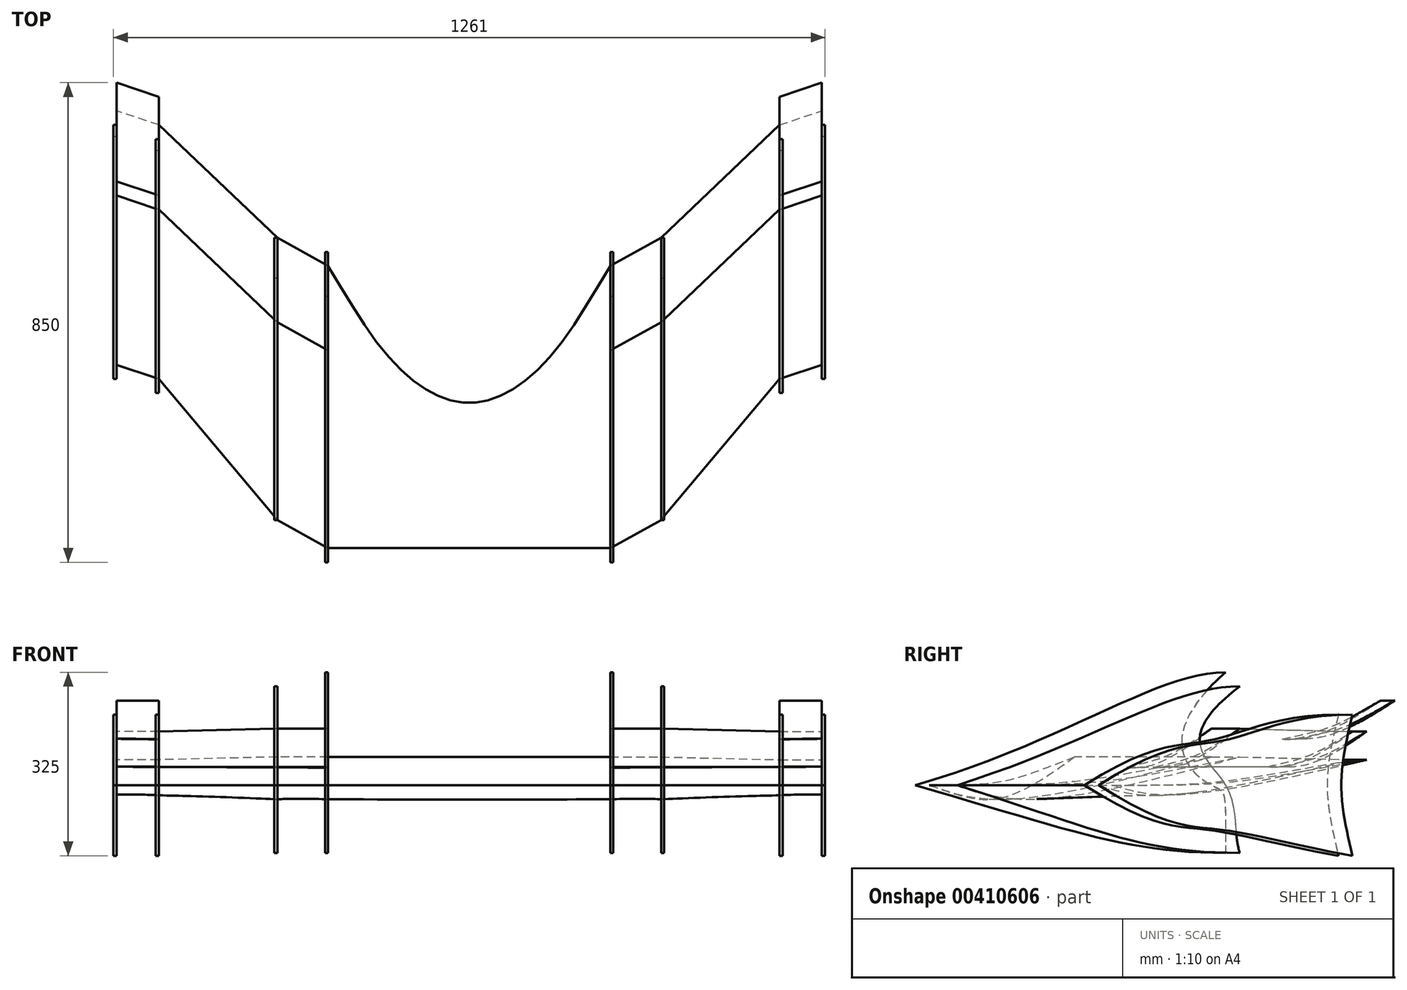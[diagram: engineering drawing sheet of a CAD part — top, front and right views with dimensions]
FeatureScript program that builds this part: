
annotation { "Feature Type Name" : "Feature", "Feature Type Description" : "" }
export const myFeature = defineFeature(function(context is Context, id is Id, definition is map)
    precondition{}
    {
        {
            var Q0;
            Q0=qCreatedBy(makeId("Right.planeOp"),FACE);
            cPlane(context, id + "F0", {"entities" : qUnion([Q0]), "cplaneType" : CPlaneType.OFFSET, "offset" : 250 * mm, "width" : 150 * mm, "height" : 150 * mm});
        }
        {
            var Q0;
            Q0=qCreatedBy(id+"F0.planeOp",FACE);
            var sketch = newSketch(context, id + "F1", { "sketchPlane" : qUnion([Q0])});
            skPoint(sketch, "E0.middle", {"position": v(0, 0) * mm});
            skFitSpline(sketch, "E1", {"points": [v(-275, 0) * mm, v(275, 200) * mm], "startDerivative": vector(825, 240) * mm, "endDerivative": vector(375, 0) * mm});
            skFitSpline(sketch, "E2", {"points": [v(275, 200) * mm, v(250, 0) * mm, v(275, -120) * mm], "startDerivative": vector(-734.18, -640.74) * mm, "endDerivative": vector(0, -821.63) * mm});
            skFitSpline(sketch, "E3", {"points": [v(-275, 0) * mm, v(275, -120) * mm], "startDerivative": vector(825, -240) * mm, "endDerivative": vector(525, 0) * mm});
            skSolve(sketch);
        }
        {
            var Q0;
            Q0=qCreatedBy(makeId("Right.planeOp"),FACE);
            cPlane(context, id + "F2", {"entities" : qUnion([Q0]), "cplaneType" : CPlaneType.OFFSET, "offset" : 340 * mm, "width" : 150 * mm, "height" : 150 * mm});
        }
        {
            var Q0;
            Q0=qCreatedBy(id+"F2.planeOp",FACE);
            var sketch = newSketch(context, id + "F3", { "sketchPlane" : qUnion([Q0])});
            skFitSpline(sketch, "E4", {"points": [v(-200, 0) * mm, v(300, 175) * mm], "startDerivative": vector(750, 240) * mm, "endDerivative": vector(375, 0) * mm});
            skFitSpline(sketch, "E5", {"points": [v(300, 175) * mm, v(275, 0) * mm, v(300, -120) * mm], "startDerivative": vector(-687.26, -522.32) * mm, "endDerivative": vector(77.93, -251.25) * mm});
            skFitSpline(sketch, "E6", {"points": [v(-200, 0) * mm, v(300, -120) * mm], "startDerivative": vector(750, -240) * mm, "endDerivative": vector(525, 0) * mm});
            skSolve(sketch);
        }
        {
            var Q0;
            Q0=qCreatedBy(makeId("Right.planeOp"),FACE);
            cPlane(context, id + "F4", {"entities" : qUnion([Q0]), "cplaneType" : CPlaneType.OFFSET, "offset" : 550 * mm, "width" : 150 * mm, "height" : 150 * mm});
        }
        {
            var Q0;
            Q0=qCreatedBy(id+"F4.planeOp",FACE);
            var sketch = newSketch(context, id + "F5", { "sketchPlane" : qUnion([Q0])});
            skFitSpline(sketch, "E7", {"points": [v(25, 0) * mm, v(250, 80) * mm, v(475, 125) * mm], "startDerivative": vector(742.6, 475.26) * mm, "endDerivative": vector(681.8, 0) * mm});
            skFitSpline(sketch, "E8", {"points": [v(475, 125) * mm, v(455, 0) * mm, v(475, -125) * mm], "startDerivative": vector(-60, -250) * mm, "endDerivative": vector(60, -250) * mm});
            skFitSpline(sketch, "E9", {"points": [v(25, 0) * mm, v(250, -80) * mm, v(475, -125) * mm], "startDerivative": vector(742.6, -475.26) * mm, "endDerivative": vector(456.76, -74.2) * mm});
            skSolve(sketch);
        }
        {
            var Q0;
            Q0=qCreatedBy(makeId("Right.planeOp"),FACE);
            cPlane(context, id + "F6", {"entities" : qUnion([Q0]), "cplaneType" : CPlaneType.OFFSET, "offset" : 625 * mm, "width" : 150 * mm, "height" : 150 * mm});
        }
        {
            var Q0;
            Q0=qCreatedBy(id+"F6.planeOp",FACE);
            var sketch = newSketch(context, id + "F7", { "sketchPlane" : qUnion([Q0])});
            skFitSpline(sketch, "E10", {"points": [v(50, 0) * mm, v(275, 80) * mm, v(500, 125) * mm], "startDerivative": vector(742.6, 475.26) * mm, "endDerivative": vector(681.8, 0) * mm});
            skFitSpline(sketch, "E11", {"points": [v(500, 125) * mm, v(480, 0) * mm, v(500, -125) * mm], "startDerivative": vector(-60, -250) * mm, "endDerivative": vector(60, -250) * mm});
            skFitSpline(sketch, "E12", {"points": [v(50, 0) * mm, v(275, -80) * mm, v(500, -125) * mm], "startDerivative": vector(742.6, -475.26) * mm, "endDerivative": vector(456.76, -74.2) * mm});
            skSolve(sketch);
        }
        {
            var Q0;
            Q0=qCreatedBy(makeId("Right.planeOp"),FACE);
            cPlane(context, id + "F8", {"entities" : qUnion([Q0]), "cplaneType" : CPlaneType.OFFSET, "offset" : 160 * mm, "width" : 150 * mm, "height" : 150 * mm});
        }
        {
            var Q0;
            Q0=qCreatedBy(id+"F8.planeOp",FACE);
            var sketch = newSketch(context, id + "F9", { "sketchPlane" : qUnion([Q0])});
            skFitSpline(sketch, "E13", {"points": [v(-250, 0) * mm, v(-125, -25) * mm, v(110, 50) * mm], "startDerivative": vector(276.92, -99.23) * mm, "endDerivative": vector(434.5, 183.8) * mm});
            skFitSpline(sketch, "E14", {"points": [v(-250, 0) * mm, v(110, 50) * mm], "startDerivative": vector(540, 0) * mm, "endDerivative": vector(540, 150) * mm});
            skSolve(sketch);
        }
        {
            var Q0;
            Q0=qCreatedBy(makeId("Right.planeOp"),FACE);
            cPlane(context, id + "F10", {"entities" : qUnion([Q0]), "cplaneType" : CPlaneType.OFFSET, "offset" : 250 * mm, "width" : 150 * mm, "height" : 150 * mm});
        }
        {
            var Q0;
            Q0=qCreatedBy(id+"F10.planeOp",FACE);
            var sketch = newSketch(context, id + "F11", { "sketchPlane" : qUnion([Q0])});
            skFitSpline(sketch, "E15", {"points": [v(-250, 0) * mm, v(-125, -25) * mm, v(250, 50) * mm], "startDerivative": vector(295.75, -102.45) * mm, "endDerivative": vector(670.75, 177.45) * mm});
            skFitSpline(sketch, "E16", {"points": [v(-250, 0) * mm, v(250, 50) * mm], "startDerivative": vector(750, 0) * mm, "endDerivative": vector(750, 150) * mm});
            skSolve(sketch);
        }
        {
            var Q0;
            Q0=qCreatedBy(id+"F10.planeOp",FACE);
            var sketch = newSketch(context, id + "F12", { "sketchPlane" : qUnion([Q0])});
            skFitSpline(sketch, "E17", {"points": [v(100, 32) * mm, v(125, 32) * mm, v(250, 100) * mm], "startDerivative": vector(70.95, -14.25) * mm, "endDerivative": vector(319.3, 251.19) * mm});
            skFitSpline(sketch, "E18", {"points": [v(100, 32) * mm, v(250, 100) * mm], "startDerivative": vector(225, 54) * mm, "endDerivative": vector(225, 150) * mm});
            skSolve(sketch);
        }
        {
            var Q0;
            Q0=qCreatedBy(makeId("Right.planeOp"),FACE);
            cPlane(context, id + "F13", {"entities" : qUnion([Q0]), "cplaneType" : CPlaneType.OFFSET, "offset" : 340 * mm, "width" : 150 * mm, "height" : 150 * mm});
        }
        {
            var Q0;
            Q0=qCreatedBy(id+"F13.planeOp",FACE);
            var sketch = newSketch(context, id + "F14", { "sketchPlane" : qUnion([Q0])});
            skFitSpline(sketch, "E19", {"points": [v(-200, 0) * mm, v(-75, -25) * mm, v(300, 50) * mm], "startDerivative": vector(295.75, -102.45) * mm, "endDerivative": vector(670.75, 177.45) * mm});
            skFitSpline(sketch, "E20", {"points": [v(-200, 0) * mm, v(300, 50) * mm], "startDerivative": vector(750, 0) * mm, "endDerivative": vector(750, 150) * mm});
            skSolve(sketch);
        }
        {
            var Q0;
            Q0=qCreatedBy(id+"F13.planeOp",FACE);
            var sketch = newSketch(context, id + "F15", { "sketchPlane" : qUnion([Q0])});
            skFitSpline(sketch, "E21", {"points": [v(150, 32.5) * mm, v(175, 32.5) * mm, v(300, 100) * mm], "startDerivative": vector(70.88, -14.16) * mm, "endDerivative": vector(319.39, 250.19) * mm});
            skFitSpline(sketch, "E22", {"points": [v(150, 32.5) * mm, v(300, 100) * mm], "startDerivative": vector(225, 52.5) * mm, "endDerivative": vector(225, 150) * mm});
            skSolve(sketch);
        }
        {
            var Q0;
            Q0=qCreatedBy(makeId("Right.planeOp"),FACE);
            cPlane(context, id + "F16", {"entities" : qUnion([Q0]), "cplaneType" : CPlaneType.OFFSET, "offset" : 550 * mm, "width" : 150 * mm, "height" : 150 * mm});
        }
        {
            var Q0;
            Q0=qCreatedBy(id+"F16.planeOp",FACE);
            var sketch = newSketch(context, id + "F17", { "sketchPlane" : qUnion([Q0])});
            skFitSpline(sketch, "E23", {"points": [v(50, 0) * mm, v(150, -18) * mm, v(500, 45) * mm], "startDerivative": vector(243.54, -77.51) * mm, "endDerivative": vector(618.54, 145.01) * mm});
            skFitSpline(sketch, "E24", {"points": [v(50, 0) * mm, v(500, 45) * mm], "startDerivative": vector(600, 0) * mm, "endDerivative": vector(750, 135) * mm});
            skSolve(sketch);
        }
        {
            var Q0;
            Q0=qCreatedBy(id+"F16.planeOp",FACE);
            var sketch = newSketch(context, id + "F18", { "sketchPlane" : qUnion([Q0])});
            skFitSpline(sketch, "E25", {"points": [v(350, 33) * mm, v(375, 33) * mm, v(500, 95) * mm], "startDerivative": vector(70.1, -13.12) * mm, "endDerivative": vector(320.24, 228.44) * mm});
            skFitSpline(sketch, "E26", {"points": [v(350, 33) * mm, v(500, 95) * mm], "startDerivative": vector(225, 51) * mm, "endDerivative": vector(225, 135) * mm});
            skSolve(sketch);
        }
        {
            var Q0;
            Q0=qCreatedBy(id+"F16.planeOp",FACE);
            var sketch = newSketch(context, id + "F19", { "sketchPlane" : qUnion([Q0])});
            skFitSpline(sketch, "E27", {"points": [v(375, 82) * mm, v(400, 82) * mm, v(550, 150) * mm], "startDerivative": vector(72.45, -13.25) * mm, "endDerivative": vector(364.77, 245.96) * mm});
            skFitSpline(sketch, "E28", {"points": [v(375, 82) * mm, v(550, 150) * mm], "startDerivative": vector(262.5, 54) * mm, "endDerivative": vector(262.5, 150) * mm});
            skSolve(sketch);
        }
        {
            var Q0;
            Q0=qCreatedBy(makeId("Right.planeOp"),FACE);
            cPlane(context, id + "F20", {"entities" : qUnion([Q0]), "cplaneType" : CPlaneType.OFFSET, "offset" : 625 * mm, "width" : 150 * mm, "height" : 150 * mm});
        }
        {
            var Q0;
            Q0=qCreatedBy(id+"F20.planeOp",FACE);
            var sketch = newSketch(context, id + "F21", { "sketchPlane" : qUnion([Q0])});
            skFitSpline(sketch, "E29", {"points": [v(75, 0) * mm, v(175, -17) * mm, v(525, 45) * mm], "startDerivative": vector(243.71, -73.88) * mm, "endDerivative": vector(618.37, 142.03) * mm});
            skFitSpline(sketch, "E30", {"points": [v(75, 0) * mm, v(525, 45) * mm], "startDerivative": vector(600, 0) * mm, "endDerivative": vector(750, 135) * mm});
            skSolve(sketch);
        }
        {
            var Q0;
            Q0=qCreatedBy(id+"F20.planeOp",FACE);
            var sketch = newSketch(context, id + "F22", { "sketchPlane" : qUnion([Q0])});
            skFitSpline(sketch, "E31", {"points": [v(375, 33.5) * mm, v(400, 33.5) * mm, v(525, 95) * mm], "startDerivative": vector(70.04, -13.03) * mm, "endDerivative": vector(320.32, 227.42) * mm});
            skFitSpline(sketch, "E32", {"points": [v(375, 33.5) * mm, v(525, 95) * mm], "startDerivative": vector(225, 49.5) * mm, "endDerivative": vector(225, 135) * mm});
            skSolve(sketch);
        }
        {
            var Q0;
            Q0=qCreatedBy(id+"F20.planeOp",FACE);
            var sketch = newSketch(context, id + "F23", { "sketchPlane" : qUnion([Q0])});
            skFitSpline(sketch, "E33", {"points": [v(400, 83) * mm, v(425, 83) * mm, v(575, 150) * mm], "startDerivative": vector(72.33, -13.07) * mm, "endDerivative": vector(364.9, 243.96) * mm});
            skFitSpline(sketch, "E34", {"points": [v(400, 83) * mm, v(575, 150) * mm], "startDerivative": vector(262.5, 51) * mm, "endDerivative": vector(262.5, 150) * mm});
            skSolve(sketch);
        }
        {
            var Q0;
            Q0=qCreatedBy(makeId("Right.planeOp"),FACE);
            cPlane(context, id + "F24", {"entities" : qUnion([Q0]), "cplaneType" : CPlaneType.OFFSET, "offset" : 250 * mm, "oppositeDirection" : true, "width" : 150 * mm, "height" : 150 * mm});
        }
        {
            var Q0;
            Q0=qCreatedBy(id+"F24.planeOp",FACE);
            var sketch = newSketch(context, id + "F25", { "sketchPlane" : qUnion([Q0])});
            skPoint(sketch, "E35.middle", {"position": v(0, 0) * mm});
            skFitSpline(sketch, "E36", {"points": [v(-275, 0) * mm, v(275, 200) * mm], "startDerivative": vector(825, 240) * mm, "endDerivative": vector(375, 0) * mm});
            skFitSpline(sketch, "E37", {"points": [v(275, 200) * mm, v(250, 0) * mm, v(275, -120) * mm], "startDerivative": vector(-734.18, -640.74) * mm, "endDerivative": vector(0, -821.63) * mm});
            skFitSpline(sketch, "E38", {"points": [v(-275, 0) * mm, v(275, -120) * mm], "startDerivative": vector(825, -240) * mm, "endDerivative": vector(525, 0) * mm});
            skSolve(sketch);
        }
        {
            var Q0;
            Q0=qCreatedBy(makeId("Right.planeOp"),FACE);
            cPlane(context, id + "F26", {"entities" : qUnion([Q0]), "cplaneType" : CPlaneType.OFFSET, "offset" : 340 * mm, "oppositeDirection" : true, "width" : 150 * mm, "height" : 150 * mm});
        }
        {
            var Q0;
            Q0=qCreatedBy(id+"F26.planeOp",FACE);
            var sketch = newSketch(context, id + "F27", { "sketchPlane" : qUnion([Q0])});
            skFitSpline(sketch, "E39", {"points": [v(-200, 0) * mm, v(300, 175) * mm], "startDerivative": vector(750, 240) * mm, "endDerivative": vector(375, 0) * mm});
            skFitSpline(sketch, "E40", {"points": [v(300, 175) * mm, v(275, 0) * mm, v(300, -120) * mm], "startDerivative": vector(-687.26, -522.32) * mm, "endDerivative": vector(77.93, -251.25) * mm});
            skFitSpline(sketch, "E41", {"points": [v(-200, 0) * mm, v(300, -120) * mm], "startDerivative": vector(750, -240) * mm, "endDerivative": vector(525, 0) * mm});
            skSolve(sketch);
        }
        {
            var Q0;
            Q0=qCreatedBy(makeId("Right.planeOp"),FACE);
            cPlane(context, id + "F28", {"entities" : qUnion([Q0]), "cplaneType" : CPlaneType.OFFSET, "offset" : 550 * mm, "oppositeDirection" : true, "width" : 150 * mm, "height" : 150 * mm});
        }
        {
            var Q0;
            Q0=qCreatedBy(id+"F28.planeOp",FACE);
            var sketch = newSketch(context, id + "F29", { "sketchPlane" : qUnion([Q0])});
            skFitSpline(sketch, "E42", {"points": [v(25, 0) * mm, v(250, 80) * mm, v(475, 125) * mm], "startDerivative": vector(742.6, 475.26) * mm, "endDerivative": vector(681.8, 0) * mm});
            skFitSpline(sketch, "E43", {"points": [v(475, 125) * mm, v(455, 0) * mm, v(475, -125) * mm], "startDerivative": vector(-60, -250) * mm, "endDerivative": vector(60, -250) * mm});
            skFitSpline(sketch, "E44", {"points": [v(25, 0) * mm, v(250, -80) * mm, v(475, -125) * mm], "startDerivative": vector(742.6, -475.26) * mm, "endDerivative": vector(456.76, -74.2) * mm});
            skSolve(sketch);
        }
        {
            var Q0;
            Q0=qCreatedBy(makeId("Right.planeOp"),FACE);
            cPlane(context, id + "F30", {"entities" : qUnion([Q0]), "cplaneType" : CPlaneType.OFFSET, "offset" : 625 * mm, "oppositeDirection" : true, "width" : 150 * mm, "height" : 150 * mm});
        }
        {
            var Q0;
            Q0=qCreatedBy(id+"F30.planeOp",FACE);
            var sketch = newSketch(context, id + "F31", { "sketchPlane" : qUnion([Q0])});
            skFitSpline(sketch, "E45", {"points": [v(50, 0) * mm, v(275, 80) * mm, v(500, 125) * mm], "startDerivative": vector(742.6, 475.26) * mm, "endDerivative": vector(681.8, 0) * mm});
            skFitSpline(sketch, "E46", {"points": [v(500, 125) * mm, v(480, 0) * mm, v(500, -125) * mm], "startDerivative": vector(-60, -250) * mm, "endDerivative": vector(60, -250) * mm});
            skFitSpline(sketch, "E47", {"points": [v(50, 0) * mm, v(275, -80) * mm, v(500, -125) * mm], "startDerivative": vector(742.6, -475.26) * mm, "endDerivative": vector(456.76, -74.2) * mm});
            skSolve(sketch);
        }
        {
            var Q0;
            Q0=qCreatedBy(makeId("Right.planeOp"),FACE);
            cPlane(context, id + "F32", {"entities" : qUnion([Q0]), "cplaneType" : CPlaneType.OFFSET, "offset" : 160 * mm, "oppositeDirection" : true, "width" : 150 * mm, "height" : 150 * mm});
        }
        {
            var Q0;
            Q0=qCreatedBy(id+"F32.planeOp",FACE);
            var sketch = newSketch(context, id + "F33", { "sketchPlane" : qUnion([Q0])});
            skFitSpline(sketch, "E48", {"points": [v(-250, 0) * mm, v(-125, -25) * mm, v(110, 50) * mm], "startDerivative": vector(276.92, -99.23) * mm, "endDerivative": vector(434.5, 183.8) * mm});
            skFitSpline(sketch, "E49", {"points": [v(-250, 0) * mm, v(110, 50) * mm], "startDerivative": vector(540, 0) * mm, "endDerivative": vector(540, 150) * mm});
            skSolve(sketch);
        }
        {
            var Q0;
            Q0=qCreatedBy(makeId("Right.planeOp"),FACE);
            cPlane(context, id + "F34", {"entities" : qUnion([Q0]), "cplaneType" : CPlaneType.OFFSET, "offset" : 250 * mm, "oppositeDirection" : true, "width" : 150 * mm, "height" : 150 * mm});
        }
        {
            var Q0;
            Q0=qCreatedBy(id+"F34.planeOp",FACE);
            var sketch = newSketch(context, id + "F35", { "sketchPlane" : qUnion([Q0])});
            skFitSpline(sketch, "E50", {"points": [v(-250, 0) * mm, v(-125, -25) * mm, v(250, 50) * mm], "startDerivative": vector(295.75, -102.45) * mm, "endDerivative": vector(670.75, 177.45) * mm});
            skFitSpline(sketch, "E51", {"points": [v(-250, 0) * mm, v(250, 50) * mm], "startDerivative": vector(750, 0) * mm, "endDerivative": vector(750, 150) * mm});
            skSolve(sketch);
        }
        {
            var Q0;
            Q0=qCreatedBy(id+"F34.planeOp",FACE);
            var sketch = newSketch(context, id + "F36", { "sketchPlane" : qUnion([Q0])});
            skFitSpline(sketch, "E52", {"points": [v(100, 32) * mm, v(125, 32) * mm, v(250, 100) * mm], "startDerivative": vector(70.95, -14.25) * mm, "endDerivative": vector(319.3, 251.19) * mm});
            skFitSpline(sketch, "E53", {"points": [v(100, 32) * mm, v(250, 100) * mm], "startDerivative": vector(225, 54) * mm, "endDerivative": vector(225, 150) * mm});
            skSolve(sketch);
        }
        {
            var Q0;
            Q0=qCreatedBy(makeId("Right.planeOp"),FACE);
            cPlane(context, id + "F37", {"entities" : qUnion([Q0]), "cplaneType" : CPlaneType.OFFSET, "offset" : 340 * mm, "oppositeDirection" : true, "width" : 150 * mm, "height" : 150 * mm});
        }
        {
            var Q0;
            Q0=qCreatedBy(id+"F37.planeOp",FACE);
            var sketch = newSketch(context, id + "F38", { "sketchPlane" : qUnion([Q0])});
            skFitSpline(sketch, "E54", {"points": [v(-200, 0) * mm, v(-75, -25) * mm, v(300, 50) * mm], "startDerivative": vector(295.75, -102.45) * mm, "endDerivative": vector(670.75, 177.45) * mm});
            skFitSpline(sketch, "E55", {"points": [v(-200, 0) * mm, v(300, 50) * mm], "startDerivative": vector(750, 0) * mm, "endDerivative": vector(750, 150) * mm});
            skSolve(sketch);
        }
        {
            var Q0;
            Q0=qCreatedBy(id+"F37.planeOp",FACE);
            var sketch = newSketch(context, id + "F39", { "sketchPlane" : qUnion([Q0])});
            skFitSpline(sketch, "E56", {"points": [v(150, 32.5) * mm, v(175, 32.5) * mm, v(300, 100) * mm], "startDerivative": vector(70.88, -14.16) * mm, "endDerivative": vector(319.39, 250.19) * mm});
            skFitSpline(sketch, "E57", {"points": [v(150, 32.5) * mm, v(300, 100) * mm], "startDerivative": vector(225, 52.5) * mm, "endDerivative": vector(225, 150) * mm});
            skSolve(sketch);
        }
        {
            var Q0;
            Q0=qCreatedBy(makeId("Right.planeOp"),FACE);
            cPlane(context, id + "F40", {"entities" : qUnion([Q0]), "cplaneType" : CPlaneType.OFFSET, "offset" : 550 * mm, "oppositeDirection" : true, "width" : 150 * mm, "height" : 150 * mm});
        }
        {
            var Q0;
            Q0=qCreatedBy(id+"F40.planeOp",FACE);
            var sketch = newSketch(context, id + "F41", { "sketchPlane" : qUnion([Q0])});
            skFitSpline(sketch, "E58", {"points": [v(50, 0) * mm, v(150, -18) * mm, v(500, 45) * mm], "startDerivative": vector(243.54, -77.51) * mm, "endDerivative": vector(618.54, 145.01) * mm});
            skFitSpline(sketch, "E59", {"points": [v(50, 0) * mm, v(500, 45) * mm], "startDerivative": vector(600, 0) * mm, "endDerivative": vector(750, 135) * mm});
            skSolve(sketch);
        }
        {
            var Q0;
            Q0=qCreatedBy(id+"F40.planeOp",FACE);
            var sketch = newSketch(context, id + "F42", { "sketchPlane" : qUnion([Q0])});
            skFitSpline(sketch, "E60", {"points": [v(350, 33) * mm, v(375, 33) * mm, v(500, 95) * mm], "startDerivative": vector(70.1, -13.12) * mm, "endDerivative": vector(320.24, 228.44) * mm});
            skFitSpline(sketch, "E61", {"points": [v(350, 33) * mm, v(500, 95) * mm], "startDerivative": vector(225, 51) * mm, "endDerivative": vector(225, 135) * mm});
            skSolve(sketch);
        }
        {
            var Q0;
            Q0=qCreatedBy(id+"F40.planeOp",FACE);
            var sketch = newSketch(context, id + "F43", { "sketchPlane" : qUnion([Q0])});
            skFitSpline(sketch, "E62", {"points": [v(375, 82) * mm, v(400, 82) * mm, v(550, 150) * mm], "startDerivative": vector(72.45, -13.25) * mm, "endDerivative": vector(364.77, 245.96) * mm});
            skFitSpline(sketch, "E63", {"points": [v(375, 82) * mm, v(550, 150) * mm], "startDerivative": vector(262.5, 54) * mm, "endDerivative": vector(262.5, 150) * mm});
            skSolve(sketch);
        }
        {
            var Q0;
            Q0=qCreatedBy(makeId("Right.planeOp"),FACE);
            cPlane(context, id + "F44", {"entities" : qUnion([Q0]), "cplaneType" : CPlaneType.OFFSET, "offset" : 625 * mm, "oppositeDirection" : true, "width" : 150 * mm, "height" : 150 * mm});
        }
        {
            var Q0;
            Q0=qCreatedBy(id+"F44.planeOp",FACE);
            var sketch = newSketch(context, id + "F45", { "sketchPlane" : qUnion([Q0])});
            skFitSpline(sketch, "E64", {"points": [v(75, 0) * mm, v(175, -17) * mm, v(525, 45) * mm], "startDerivative": vector(243.71, -73.88) * mm, "endDerivative": vector(618.37, 142.03) * mm});
            skFitSpline(sketch, "E65", {"points": [v(75, 0) * mm, v(525, 45) * mm], "startDerivative": vector(600, 0) * mm, "endDerivative": vector(750, 135) * mm});
            skSolve(sketch);
        }
        {
            var Q0;
            Q0=qCreatedBy(id+"F44.planeOp",FACE);
            var sketch = newSketch(context, id + "F46", { "sketchPlane" : qUnion([Q0])});
            skFitSpline(sketch, "E66", {"points": [v(375, 33.5) * mm, v(400, 33.5) * mm, v(525, 95) * mm], "startDerivative": vector(70.04, -13.03) * mm, "endDerivative": vector(320.32, 227.42) * mm});
            skFitSpline(sketch, "E67", {"points": [v(375, 33.5) * mm, v(525, 95) * mm], "startDerivative": vector(225, 49.5) * mm, "endDerivative": vector(225, 135) * mm});
            skSolve(sketch);
        }
        {
            var Q0;
            Q0=qCreatedBy(id+"F44.planeOp",FACE);
            var sketch = newSketch(context, id + "F47", { "sketchPlane" : qUnion([Q0])});
            skFitSpline(sketch, "E68", {"points": [v(400, 83) * mm, v(425, 83) * mm, v(575, 150) * mm], "startDerivative": vector(72.33, -13.07) * mm, "endDerivative": vector(364.9, 243.96) * mm});
            skFitSpline(sketch, "E69", {"points": [v(400, 83) * mm, v(575, 150) * mm], "startDerivative": vector(262.5, 51) * mm, "endDerivative": vector(262.5, 150) * mm});
            skSolve(sketch);
        }
        {
            var Q0;
            Q0=makeQuery(id+"F35.imprint","IMPRINT",FACE,{"disambiguationData":[TD([[makeQuery(id+"F35.imprint","IMPRINT",EDGE,{"derivedFrom":sQuery(id+"F35.wireOp",EDGE,"E50")}),1.0]])]});
            var Q1;
            Q1=makeQuery(id+"F33.imprint","IMPRINT",FACE,{"disambiguationData":[TD([[makeQuery(id+"F33.imprint","IMPRINT",EDGE,{"derivedFrom":sQuery(id+"F33.wireOp",EDGE,"E48")}),1.0]])]});
            var Q2;
            Q2=makeQuery(id+"F9.imprint","IMPRINT",FACE,{"disambiguationData":[TD([[makeQuery(id+"F9.imprint","IMPRINT",EDGE,{"derivedFrom":sQuery(id+"F9.wireOp",EDGE,"E13")}),1.0]])]});
            var Q3;
            Q3=makeQuery(id+"F11.imprint","IMPRINT",FACE,{"disambiguationData":[TD([[makeQuery(id+"F11.imprint","IMPRINT",EDGE,{"derivedFrom":sQuery(id+"F11.wireOp",EDGE,"E15")}),1.0]])]});
            loft(context, id + "F48", {"sheetProfilesArray" : [{ "sheetProfileEntities" : qUnion([Q0]) }, { "sheetProfileEntities" : qUnion([Q1]) }, { "sheetProfileEntities" : qUnion([Q2]) }, { "sheetProfileEntities" : qUnion([Q3]) }]});
        }
        {
            var Q1;
            Q1=makeQuery(id+"F48.opLoft","CAP_FACE",FACE,{"disambiguationData":[OSD([makeQuery(id+"F35.imprint","IMPRINT",FACE,{"disambiguationData":[TD([[makeQuery(id+"F35.imprint","IMPRINT",EDGE,{"derivedFrom":sQuery(id+"F35.wireOp",EDGE,"E50")}),1.0]])]})])],"isStart":true});
            var Q2;
            Q2=makeQuery(id+"F38.imprint","IMPRINT",FACE,{"disambiguationData":[TD([[makeQuery(id+"F38.imprint","IMPRINT",EDGE,{"derivedFrom":sQuery(id+"F38.wireOp",EDGE,"E54")}),1.0]])]});
            loft(context, id + "F49", {"operationType" : NewBodyOperationType.ADD, "sheetProfilesArray" : [{ "sheetProfileEntities" : qUnion([Q1]) }, { "sheetProfileEntities" : qUnion([Q2]) }]});
        }
        {
            var Q1;
            Q1=makeQuery(id+"F48.opLoft","CAP_FACE",FACE,{"disambiguationData":[OSD([makeQuery(id+"F11.imprint","IMPRINT",FACE,{"disambiguationData":[TD([[makeQuery(id+"F11.imprint","IMPRINT",EDGE,{"derivedFrom":sQuery(id+"F11.wireOp",EDGE,"E15")}),1.0]])]})])],"isStart":true});
            var Q2;
            Q2=makeQuery(id+"F14.imprint","IMPRINT",FACE,{"disambiguationData":[TD([[makeQuery(id+"F14.imprint","IMPRINT",EDGE,{"derivedFrom":sQuery(id+"F14.wireOp",EDGE,"E19")}),1.0]])]});
            loft(context, id + "F50", {"operationType" : NewBodyOperationType.ADD, "sheetProfilesArray" : [{ "sheetProfileEntities" : qUnion([Q1]) }, { "sheetProfileEntities" : qUnion([Q2]) }]});
        }
        {
            var Q1;
            Q1=makeQuery(id+"F49.opLoft","CAP_FACE",FACE,{"disambiguationData":[OSD([makeQuery(id+"F38.imprint","IMPRINT",FACE,{"disambiguationData":[TD([[makeQuery(id+"F38.imprint","IMPRINT",EDGE,{"derivedFrom":sQuery(id+"F38.wireOp",EDGE,"E54")}),1.0]])]})])],"isStart":true});
            var Q2;
            Q2=makeQuery(id+"F41.imprint","IMPRINT",FACE,{"disambiguationData":[TD([[makeQuery(id+"F41.imprint","IMPRINT",EDGE,{"derivedFrom":sQuery(id+"F41.wireOp",EDGE,"E58")}),1.0]])]});
            loft(context, id + "F51", {"operationType" : NewBodyOperationType.ADD, "sheetProfilesArray" : [{ "sheetProfileEntities" : qUnion([Q1]) }, { "sheetProfileEntities" : qUnion([Q2]) }]});
        }
        {
            var Q1;
            Q1=makeQuery(id+"F50.opLoft","CAP_FACE",FACE,{"disambiguationData":[OSD([makeQuery(id+"F14.imprint","IMPRINT",FACE,{"disambiguationData":[TD([[makeQuery(id+"F14.imprint","IMPRINT",EDGE,{"derivedFrom":sQuery(id+"F14.wireOp",EDGE,"E19")}),1.0]])]})])],"isStart":true});
            var Q2;
            Q2=makeQuery(id+"F17.imprint","IMPRINT",FACE,{"disambiguationData":[TD([[makeQuery(id+"F17.imprint","IMPRINT",EDGE,{"derivedFrom":sQuery(id+"F17.wireOp",EDGE,"E23")}),1.0]])]});
            loft(context, id + "F52", {"operationType" : NewBodyOperationType.ADD, "sheetProfilesArray" : [{ "sheetProfileEntities" : qUnion([Q1]) }, { "sheetProfileEntities" : qUnion([Q2]) }]});
        }
        {
            var Q1;
            Q1=makeQuery(id+"F51.opLoft","CAP_FACE",FACE,{"disambiguationData":[OSD([makeQuery(id+"F41.imprint","IMPRINT",FACE,{"disambiguationData":[TD([[makeQuery(id+"F41.imprint","IMPRINT",EDGE,{"derivedFrom":sQuery(id+"F41.wireOp",EDGE,"E58")}),1.0]])]})])],"isStart":true});
            var Q2;
            Q2=makeQuery(id+"F45.imprint","IMPRINT",FACE,{"disambiguationData":[TD([[makeQuery(id+"F45.imprint","IMPRINT",EDGE,{"derivedFrom":sQuery(id+"F45.wireOp",EDGE,"E64")}),1.0]])]});
            loft(context, id + "F53", {"operationType" : NewBodyOperationType.ADD, "sheetProfilesArray" : [{ "sheetProfileEntities" : qUnion([Q1]) }, { "sheetProfileEntities" : qUnion([Q2]) }]});
        }
        {
            var Q1;
            Q1=makeQuery(id+"F52.opLoft","CAP_FACE",FACE,{"disambiguationData":[OSD([makeQuery(id+"F17.imprint","IMPRINT",FACE,{"disambiguationData":[TD([[makeQuery(id+"F17.imprint","IMPRINT",EDGE,{"derivedFrom":sQuery(id+"F17.wireOp",EDGE,"E23")}),1.0]])]})])],"isStart":true});
            var Q2;
            Q2=makeQuery(id+"F21.imprint","IMPRINT",FACE,{"disambiguationData":[TD([[makeQuery(id+"F21.imprint","IMPRINT",EDGE,{"derivedFrom":sQuery(id+"F21.wireOp",EDGE,"E29")}),1.0]])]});
            loft(context, id + "F54", {"operationType" : NewBodyOperationType.ADD, "sheetProfilesArray" : [{ "sheetProfileEntities" : qUnion([Q1]) }, { "sheetProfileEntities" : qUnion([Q2]) }]});
        }
        {
            var Q0;
            Q0=makeQuery(id+"F36.imprint","IMPRINT",FACE,{"disambiguationData":[TD([[makeQuery(id+"F36.imprint","IMPRINT",EDGE,{"derivedFrom":sQuery(id+"F36.wireOp",EDGE,"E52")}),1.0]])]});
            var Q1;
            Q1=makeQuery(id+"F39.imprint","IMPRINT",FACE,{"disambiguationData":[TD([[makeQuery(id+"F39.imprint","IMPRINT",EDGE,{"derivedFrom":sQuery(id+"F39.wireOp",EDGE,"E56")}),1.0]])]});
            loft(context, id + "F55", {"sheetProfilesArray" : [{ "sheetProfileEntities" : qUnion([Q0]) }, { "sheetProfileEntities" : qUnion([Q1]) }]});
        }
        {
            var Q0;
            Q0=makeQuery(id+"F12.imprint","IMPRINT",FACE,{"disambiguationData":[TD([[makeQuery(id+"F12.imprint","IMPRINT",EDGE,{"derivedFrom":sQuery(id+"F12.wireOp",EDGE,"E17")}),1.0]])]});
            var Q1;
            Q1=makeQuery(id+"F15.imprint","IMPRINT",FACE,{"disambiguationData":[TD([[makeQuery(id+"F15.imprint","IMPRINT",EDGE,{"derivedFrom":sQuery(id+"F15.wireOp",EDGE,"E21")}),1.0]])]});
            loft(context, id + "F56", {"sheetProfilesArray" : [{ "sheetProfileEntities" : qUnion([Q0]) }, { "sheetProfileEntities" : qUnion([Q1]) }]});
        }
        {
            var Q1;
            Q1=makeQuery(id+"F55.opLoft","CAP_FACE",FACE,{"disambiguationData":[OSD([makeQuery(id+"F39.imprint","IMPRINT",FACE,{"disambiguationData":[TD([[makeQuery(id+"F39.imprint","IMPRINT",EDGE,{"derivedFrom":sQuery(id+"F39.wireOp",EDGE,"E56")}),1.0]])]})])],"isStart":true});
            var Q2;
            Q2=makeQuery(id+"F42.imprint","IMPRINT",FACE,{"disambiguationData":[TD([[makeQuery(id+"F42.imprint","IMPRINT",EDGE,{"derivedFrom":sQuery(id+"F42.wireOp",EDGE,"E60")}),1.0]])]});
            loft(context, id + "F57", {"operationType" : NewBodyOperationType.ADD, "sheetProfilesArray" : [{ "sheetProfileEntities" : qUnion([Q1]) }, { "sheetProfileEntities" : qUnion([Q2]) }]});
        }
        {
            var Q1;
            Q1=makeQuery(id+"F56.opLoft","CAP_FACE",FACE,{"disambiguationData":[OSD([makeQuery(id+"F15.imprint","IMPRINT",FACE,{"disambiguationData":[TD([[makeQuery(id+"F15.imprint","IMPRINT",EDGE,{"derivedFrom":sQuery(id+"F15.wireOp",EDGE,"E21")}),1.0]])]})])],"isStart":true});
            var Q2;
            Q2=makeQuery(id+"F18.imprint","IMPRINT",FACE,{"disambiguationData":[TD([[makeQuery(id+"F18.imprint","IMPRINT",EDGE,{"derivedFrom":sQuery(id+"F18.wireOp",EDGE,"E25")}),1.0]])]});
            loft(context, id + "F58", {"operationType" : NewBodyOperationType.ADD, "sheetProfilesArray" : [{ "sheetProfileEntities" : qUnion([Q1]) }, { "sheetProfileEntities" : qUnion([Q2]) }]});
        }
        {
            var Q1;
            Q1=makeQuery(id+"F57.opLoft","CAP_FACE",FACE,{"disambiguationData":[OSD([makeQuery(id+"F42.imprint","IMPRINT",FACE,{"disambiguationData":[TD([[makeQuery(id+"F42.imprint","IMPRINT",EDGE,{"derivedFrom":sQuery(id+"F42.wireOp",EDGE,"E60")}),1.0]])]})])],"isStart":true});
            var Q2;
            Q2=makeQuery(id+"F46.imprint","IMPRINT",FACE,{"disambiguationData":[TD([[makeQuery(id+"F46.imprint","IMPRINT",EDGE,{"derivedFrom":sQuery(id+"F46.wireOp",EDGE,"E66")}),1.0]])]});
            loft(context, id + "F59", {"operationType" : NewBodyOperationType.ADD, "sheetProfilesArray" : [{ "sheetProfileEntities" : qUnion([Q1]) }, { "sheetProfileEntities" : qUnion([Q2]) }]});
        }
        {
            var Q1;
            Q1=makeQuery(id+"F58.opLoft","CAP_FACE",FACE,{"disambiguationData":[OSD([makeQuery(id+"F18.imprint","IMPRINT",FACE,{"disambiguationData":[TD([[makeQuery(id+"F18.imprint","IMPRINT",EDGE,{"derivedFrom":sQuery(id+"F18.wireOp",EDGE,"E25")}),1.0]])]})])],"isStart":true});
            var Q2;
            Q2=makeQuery(id+"F22.imprint","IMPRINT",FACE,{"disambiguationData":[TD([[makeQuery(id+"F22.imprint","IMPRINT",EDGE,{"derivedFrom":sQuery(id+"F22.wireOp",EDGE,"E31")}),1.0]])]});
            loft(context, id + "F60", {"operationType" : NewBodyOperationType.ADD, "sheetProfilesArray" : [{ "sheetProfileEntities" : qUnion([Q1]) }, { "sheetProfileEntities" : qUnion([Q2]) }]});
        }
        {
            var Q0;
            Q0=makeQuery(id+"F43.imprint","IMPRINT",FACE,{"disambiguationData":[TD([[makeQuery(id+"F43.imprint","IMPRINT",EDGE,{"derivedFrom":sQuery(id+"F43.wireOp",EDGE,"E62")}),1.0]])]});
            var Q1;
            Q1=makeQuery(id+"F47.imprint","IMPRINT",FACE,{"disambiguationData":[TD([[makeQuery(id+"F47.imprint","IMPRINT",EDGE,{"derivedFrom":sQuery(id+"F47.wireOp",EDGE,"E68")}),1.0]])]});
            loft(context, id + "F61", {"sheetProfilesArray" : [{ "sheetProfileEntities" : qUnion([Q0]) }, { "sheetProfileEntities" : qUnion([Q1]) }]});
        }
        {
            var Q0;
            Q0=makeQuery(id+"F19.imprint","IMPRINT",FACE,{"disambiguationData":[TD([[makeQuery(id+"F19.imprint","IMPRINT",EDGE,{"derivedFrom":sQuery(id+"F19.wireOp",EDGE,"E27")}),1.0]])]});
            var Q1;
            Q1=makeQuery(id+"F23.imprint","IMPRINT",FACE,{"disambiguationData":[TD([[makeQuery(id+"F23.imprint","IMPRINT",EDGE,{"derivedFrom":sQuery(id+"F23.wireOp",EDGE,"E33")}),1.0]])]});
            loft(context, id + "F62", {"sheetProfilesArray" : [{ "sheetProfileEntities" : qUnion([Q0]) }, { "sheetProfileEntities" : qUnion([Q1]) }]});
        }
        {
            var Q0;
            Q0=makeQuery(id+"F25.imprint","IMPRINT",FACE,{"disambiguationData":[TD([[makeQuery(id+"F25.imprint","IMPRINT",EDGE,{"derivedFrom":sQuery(id+"F25.wireOp",EDGE,"E36")}),-1.0]])]});
            extrude(context, id + "F63", {"entities" : qUnion([Q0]), "oppositeDirection" : true, "depth" : 5.5 * mm});
        }
        {
            var Q0;
            Q0=makeQuery(id+"F1.imprint","IMPRINT",FACE,{"disambiguationData":[TD([[makeQuery(id+"F1.imprint","IMPRINT",EDGE,{"derivedFrom":sQuery(id+"F1.wireOp",EDGE,"E1")}),-1.0]])]});
            extrude(context, id + "F64", {"entities" : qUnion([Q0]), "depth" : 5.5 * mm});
        }
        {
            var Q0;
            Q0=makeQuery(id+"F27.imprint","IMPRINT",FACE,{"disambiguationData":[TD([[makeQuery(id+"F27.imprint","IMPRINT",EDGE,{"derivedFrom":sQuery(id+"F27.wireOp",EDGE,"E39")}),-1.0]])]});
            extrude(context, id + "F65", {"entities" : qUnion([Q0]), "oppositeDirection" : true, "depth" : 5.5 * mm});
        }
        {
            var Q0;
            Q0=makeQuery(id+"F3.imprint","IMPRINT",FACE,{"disambiguationData":[TD([[makeQuery(id+"F3.imprint","IMPRINT",EDGE,{"derivedFrom":sQuery(id+"F3.wireOp",EDGE,"E4")}),-1.0]])]});
            extrude(context, id + "F66", {"entities" : qUnion([Q0]), "depth" : 5.5 * mm});
        }
        {
            var Q0;
            Q0=makeQuery(id+"F29.imprint","IMPRINT",FACE,{"disambiguationData":[TD([[makeQuery(id+"F29.imprint","IMPRINT",EDGE,{"derivedFrom":sQuery(id+"F29.wireOp",EDGE,"E42")}),-1.0]])]});
            extrude(context, id + "F67", {"entities" : qUnion([Q0]), "oppositeDirection" : true, "depth" : 5.5 * mm});
        }
        {
            var Q0;
            Q0=makeQuery(id+"F5.imprint","IMPRINT",FACE,{"disambiguationData":[TD([[makeQuery(id+"F5.imprint","IMPRINT",EDGE,{"derivedFrom":sQuery(id+"F5.wireOp",EDGE,"E7")}),-1.0]])]});
            extrude(context, id + "F68", {"entities" : qUnion([Q0]), "depth" : 5.5 * mm});
        }
        {
            var Q0;
            Q0=makeQuery(id+"F31.imprint","IMPRINT",FACE,{"disambiguationData":[TD([[makeQuery(id+"F31.imprint","IMPRINT",EDGE,{"derivedFrom":sQuery(id+"F31.wireOp",EDGE,"E45")}),-1.0]])]});
            extrude(context, id + "F69", {"entities" : qUnion([Q0]), "oppositeDirection" : true, "depth" : 5.5 * mm});
        }
        {
            var Q0;
            Q0=makeQuery(id+"F7.imprint","IMPRINT",FACE,{"disambiguationData":[TD([[makeQuery(id+"F7.imprint","IMPRINT",EDGE,{"derivedFrom":sQuery(id+"F7.wireOp",EDGE,"E10")}),-1.0]])]});
            extrude(context, id + "F70", {"entities" : qUnion([Q0]), "depth" : 5.5 * mm});
        }
    });
